# Revit family: ginko_4.5
name_source: partatom
category: Lighting Fixtures
units: mm (PartAtom-declared; Revit-internal decimal feet)

## family parameters
Always vertical = No
Cut with Voids When Loaded = No
Light Source = No
OmniClass Number = 23.80.70.00
OmniClass Title = Lighting
Part Type = Normal
Room Calculation Point = No
Round Connector Dimension = Use Diameter
Shared = No
Work Plane-Based = Yes

## types (3) — shared parameters
Apparent Load = 25 VA
CCT = 3000 K
CRI = CRI80
Default Elevation = 1219 mm
Description = Outdoor Projectors
IK = IK06
IP = IP66
Lamp = LED
Manufacturer = L&L Luce&Light srl
Model = GN45
Rated Power supply = 24 V
URL = https://www.lucelight.it
Wattage = 25 W
Weight = 3.35 kg
Weight Shaper Zoom = 3.50 kg

## per-type parameters (varying)
| type | Lumen Output | Photometry |
| R9 53° 25W | 1120 lm | GN45 Light source : R9 53° 25W |
| Z9 zoom 18° 25W | 740 lm | GN45 Light source : Z9 zoom 18° 25W |
| Z9 zoom 37° 25W | 1073 lm | GN45 Light source : Z9 zoom 37° 25W |

## geometry (parser evidence)
native form markers: Sweep x1
no freeform markers — native parametric forms only
